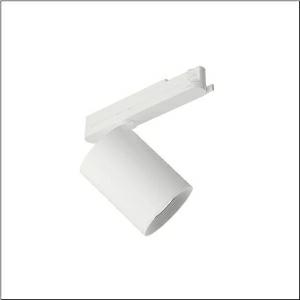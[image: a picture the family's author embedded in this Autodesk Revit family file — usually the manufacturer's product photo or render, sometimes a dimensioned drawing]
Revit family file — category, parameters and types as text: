
# Revit family: spot_11_51sd14ebd5a
name_source: partatom
category: Lighting Fixtures
units: mm (PartAtom-declared; Revit-internal decimal feet)

## family parameters
Cut with Voids When Loaded = No
Host = Face
Light Source = No
Part Type = Normal
Room Calculation Point = No
Round Connector Dimension = Use Diameter
Shared = No

## types (1)
- --- (1 x LED, 7420 lm, 51.1 W, 4000K)
    Apparent Load = 51 VA
    CIE Flux Codes = 95 98 100 100 100
    Color Rendering = 90
    Color Temperature = 4000K
    Default Elevation = 1800 mm
    Description = Spot 11, directional spotlight, light control with lens, of PMMA, LED rated luminous flux: 5.670lm, light colour: 940, control gear: ECG Multilumen, with 3-phase adapter, mains connection: 220..240V, AC, 50/60Hz, of aluminium, traffic white (RAL 9016), length: 253mm, diameter: 105mm, protection rating (complete): IP20, insulation class (complete): insulation class I (protective earthing), certification: CE, impact resistance: IK02, permissible ambient temperature for indoor applications: -20..+40°C, packaging unit: 1 piece
    Height = 175 mm
    Lamp = 1 x LED
    Lamp Light Flux = 7420 lm
    Lamp Power = 51.1 W
    Lamp count = 1
    Length = 105 mm
    Luminous efficacy = 145 lm/W
    Manufacturer = Siteco
    ModVariant = No
    Model = 51SD14EBD5A
    Mounting Place = Ceiling
    Mounting Type = Pendant
    Number of Poles = 1
    OnlyDefault = Yes
    Power Factor = 1
    Product Name = Spot 11
    Product group = directional spotlight
    ProductGroupID = 905
    Protection Class = Protection class I
    Protection Degree = IP 20
    RLX_Detail_Level = 1
    RLX_Emergency_Light_Flux = 0 lm
    RLX_Emergency_Type = 0
    RLX_Emergency_Type_DB = No
    RlxData = <blob elided: 17609 chars, md5=32b2f51e>
    Socket = socket
    Standby Power = 0 W
    System Light Flux = 7420 lm
    System Power = 51 W
    Type Comments = factory setting: luminous flux: 100 % | (ON | ON | ON | ON) | 1050 mA
    Type Image = l_1006697.jpg
    URL = http://relux.com
    VarID = @adj_146873
    Voltage = 0 V
    Weight = 0.00 kg
    Width = 0 mm  [stored 0 ft]

note: [stored X ft] marks values corroborated as IEEE doubles in the binary element streams (Revit-internal decimal feet)

## geometry (parser evidence)
native form markers: Blend x4, Sweep x10
no freeform markers — native parametric forms only
